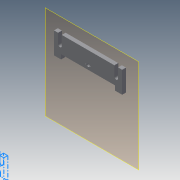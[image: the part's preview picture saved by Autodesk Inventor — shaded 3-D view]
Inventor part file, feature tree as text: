
AUTODESK INVENTOR PART (.ipt)
format: ipt  version: 2014 SP1 (Build 180222100, 222)  size: 101,888 bytes
history: native  units: in
note: dims shown in document units (in); Inventor stores cm internally (conversion verified against a paired STEP export)
features: plane x1, extrude x1, sketch x1
ambient origin geometry x8: Origin, YZ Plane, XZ Plane, XY Plane, X Axis, Y Axis, Z Axis, Center Point
bodies: Solid1 (feature_tree)
feature tree (3):
  plane  "Work Plane1"
  extrude  "Extrusion1"  Depth=6.0in
  sketch  "Sketch1"  dims[d1=3.0in d4=0.325in d7=0.3409in d8=0.0in d10=6.0in d11=0.2756in d12=0.3543in d13=0.0787in d14=0.2165in d15=0.0787in d16=0.2165in d17=2.275in]
